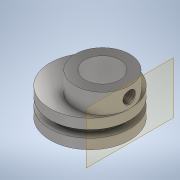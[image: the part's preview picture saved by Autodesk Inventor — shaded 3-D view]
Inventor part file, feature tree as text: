
AUTODESK INVENTOR PART (.ipt)
format: ipt  version: 2020 (Build 240168000, 168)  size: 158,720 bytes
history: native  units: mm
features: sketch x6, extrude x4, hole x2, plane x1, thread x1
ambient origin geometry x8: Origin, YZ Plane, XZ Plane, XY Plane, X Axis, Y Axis, Z Axis, Center Point
bodies: Solid1 (feature_tree)
feature tree (14):
  extrude  "Extrusion1"  Depth=2.0mm TaperAngle=0.0deg
  extrude  "Extrusion2"  Depth=1.5mm TaperAngle=0.0deg
  extrude  "Extrusion3"  Depth=2.0mm TaperAngle=0.0deg
  extrude  "Extrusion4"  Depth=4.0mm TaperAngle=0.0deg
  plane  "Work Plane1"
  hole  "Hole1"  [1 undecoded]
  thread  "Thread1"  [1 undecoded]
  hole  "Hole2"  [1 undecoded]
  sketch  "Sketch1"  dims[d0=16.0mm d1=2.0mm d2=0.0mm]
  sketch  "Sketch2"  dims[d3=13.0mm d4=1.5mm d5=0.0mm]
  sketch  "Sketch3"  dims[d6=16.0mm d7=2.0mm d8=0.0mm]
  sketch  "Sketch4"  dims[d9=11.0mm d10=4.0mm d11=0.0mm]
  sketch  "Sketch5"  dims[d12=2.0mm]
  sketch  "Sketch6"  dims[d13=2.5mm d14=6.0mm d15=4.0mm d16=2.0mm d17=90.0deg d18=2.15mm d19=20.594885mm d20=5.5mm d21=0.0mm d22=7.0mm d23=6.0mm d24=4.0mm d25=2.0mm d26=90.0deg d27=2.15mm d28=20.594885mm]
note: 3 required parameter values undecoded (feature->parameter linkage not recoverable at this tier; creation-order binding heuristic only, values carry confidence <= 0.55)
